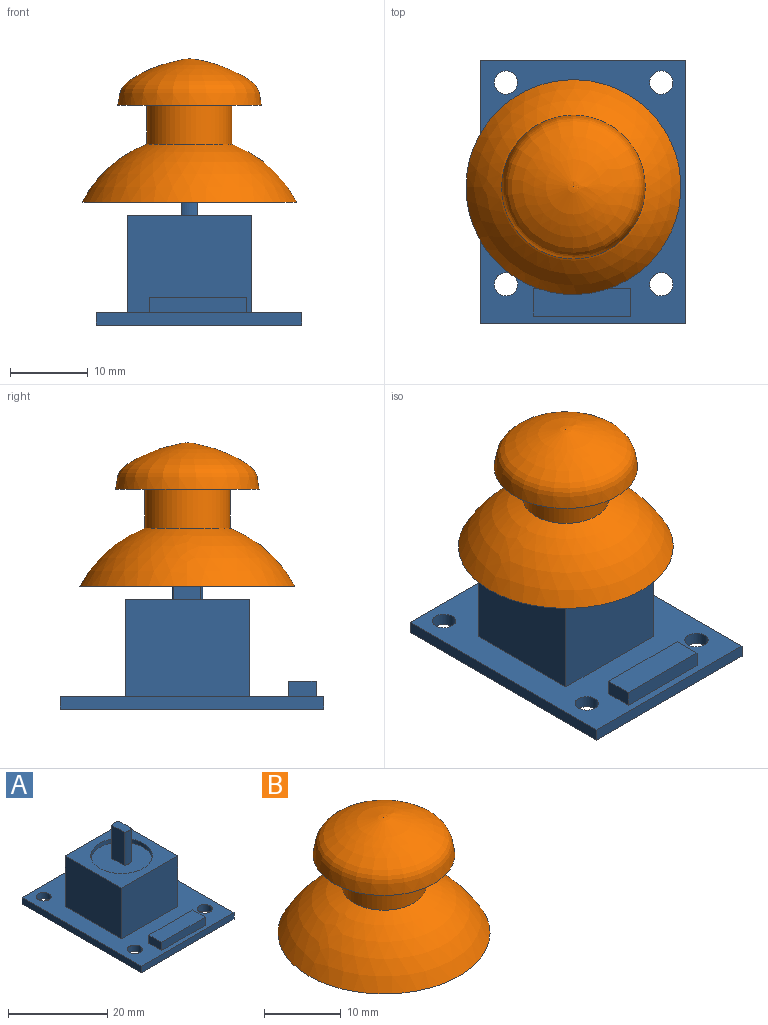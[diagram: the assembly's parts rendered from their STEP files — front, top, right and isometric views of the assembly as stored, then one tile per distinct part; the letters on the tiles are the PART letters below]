
ASSEMBLY  parts=2 mates=1
PART A: 27 faces, bbox 26.5x34x21.3 mm
  f0: plane 16x16mm, normal (0,0,1), area 135.2mm2, adj f16,f17,f18,f19,f20
  f1: plane 34x26.5mm, normal (0,0,1), area 571.7mm2, adj f2,f3,f4,f5,f6,f7,f8,f9
  f2: plane 34x1.6mm, normal (-1,0,0), area 54.4mm2, adj f1,f3,f8,f10
  f3: plane 26.5x1.6mm, normal (0,-1,0), area 42.4mm2, adj f1,f2,f4,f10
  f4: plane 34x1.6mm, normal (1,0,0), area 54.4mm2, adj f1,f3,f8,f10
  f5: cylinder r=1.5mm len=3mm, axis (0,0,-1), area 15.1mm2, adj f1,f10
  f6: cylinder r=1.5mm len=3mm, axis (0,0,-1), area 15.1mm2, adj f1,f10
  f7: cylinder r=1.5mm len=3mm, axis (0,0,-1), area 15.1mm2, adj f1,f10
  f8: plane 26.5x1.6mm, normal (0,1,0), area 42.4mm2, adj f1,f2,f4,f10
  f9: cylinder r=1.5mm len=3mm, axis (0,0,-1), area 15.1mm2, adj f1,f10
  f10: plane 34x26.5mm, normal (0,0,-1), area 872.7mm2, adj f2,f3,f4,f5,f6,f7,f8,f9
  f11: plane 12.5x2mm, normal (0,1,0), area 25mm2, adj f1,f12,f14,f15
  f12: plane 3.6x2mm, normal (-1,0,0), area 7.2mm2, adj f1,f11,f13,f15
  f13: plane 12.5x2mm, normal (0,-1,0), area 25mm2, adj f1,f12,f14,f15
  f14: plane 3.6x2mm, normal (1,0,0), area 7.2mm2, adj f1,f11,f13,f15
  f15: plane 12.5x3.6mm, normal (0,0,1), area 45mm2, adj f11,f12,f13,f14
  f16: plane 16x12.5mm, normal (0,1,0), area 200mm2, adj f0,f1,f17,f19
  f17: plane 16x12.5mm, normal (-1,0,0), area 200mm2, adj f0,f1,f16,f18
  f18: plane 16x12.5mm, normal (0,-1,0), area 200mm2, adj f0,f1,f17,f19
  f19: plane 16x12.5mm, normal (1,0,0), area 200mm2, adj f0,f1,f16,f18
  f20: cylinder r=6.2mm len=12.4mm, axis (0,0,1), area 39mm2, adj f0,f21
  f21: plane 12.4x12.4mm, normal (0,0,1), area 113.1mm2, adj f20,f23,f24,f25,f26
  f22: plane 4x2mm, normal (0,0,1), area 7.7mm2, adj f23,f24,f25,f26
  f23: plane 8.2x3.46mm, normal (-1,0,0), area 28.4mm2, adj f21,f22,f24,f26
  f24: cylinder r=2mm len=8.2mm, axis (0,0,-1), area 17.2mm2, adj f21,f22,f23,f25
  f25: plane 8.2x3.46mm, normal (1,0,0), area 28.4mm2, adj f21,f22,f24,f26
  f26: cylinder r=2mm len=8.2mm, axis (0,0,-1), area 17.2mm2, adj f21,f22,f23,f25
PART B: 10 faces, bbox 27.7x27.7x18.5 mm
  f0: plane 4x4mm, normal (0,0,-1), area 12.6mm2, adj f1
  f1: cylinder r=2mm len=5mm, axis (0,0,-1), area 62.8mm2, adj f0,f2
  f2: plane 6.5x6.5mm, normal (0,0,-1), area 20.6mm2, adj f1,f3
  f3: cylinder r=3.25mm len=6.5mm, axis (0,0,-1), area 81.7mm2, adj f2,f4
  f4: sphere r=13.9mm, area 567.7mm2, adj f3,f5
  f5: plane 27.69x27.69mm, normal (0,0,-1), area 149.9mm2, adj f4,f6
  f6: sphere r=15.52mm, area 731.4mm2, adj f5,f7
  f7: cylinder r=5.5mm len=11mm, axis (0,0,-1), area 172.8mm2, adj f6,f8
  f8: plane 18.5x18.5mm, normal (0,0,-1), area 173.8mm2, adj f7,f9
  f9: revolved ~18.5x18.5mm, area 414.1mm2, adj f8
PLACE A t=(-13.44,-5.36,-1.92)mm fixed
PLACE B t=(-1.44,12.24,16.38)mm
MATE fastened A.f20 <-> B.f1  axis (0,0,1) through (-1.44,12.24,19.38)mm
